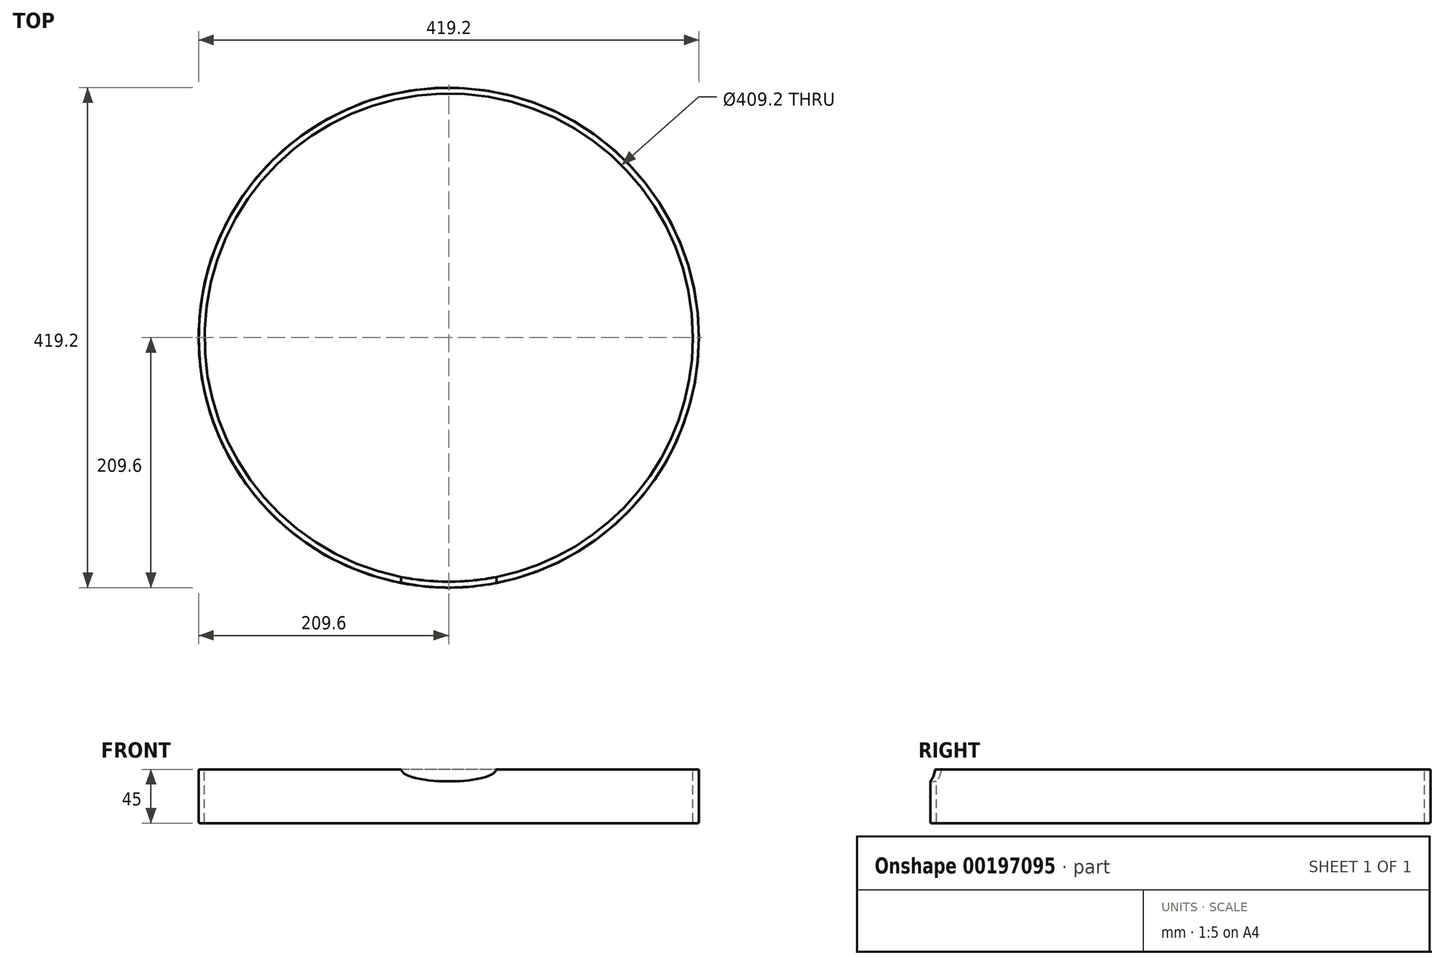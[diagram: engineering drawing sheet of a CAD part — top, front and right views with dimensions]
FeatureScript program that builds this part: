
annotation { "Feature Type Name" : "Feature", "Feature Type Description" : "" }
export const myFeature = defineFeature(function(context is Context, id is Id, definition is map)
    precondition{}
    {
        {
            var Q0;
            Q0=qCreatedBy(makeId("Front.planeOp"),FACE);
            var sketch = newSketch(context, id + "F0", { "sketchPlane" : qUnion([Q0])});
            skLineSegment(sketch, "E0", {"start": v(0, 25.64) * mm, "end": v(0, -31.1) * mm, "construction": true});
            skLineSegment(sketch, "E1", {"start": v(-208.6, 0.22) * mm, "end": v(-205.6, 0.22) * mm});
            skLineSegment(sketch, "E2", {"start": v(-204.6, -0.78) * mm, "end": v(-204.6, -43.78) * mm});
            skLineSegment(sketch, "E3", {"start": v(-209.6, -0.78) * mm, "end": v(-209.6, -43.78) * mm});
            skLineSegment(sketch, "E4", {"start": v(-208.6, -44.78) * mm, "end": v(-205.6, -44.78) * mm});
            skPoint(sketch, "E5.visualSharp", {"position": v(-204.6, 0.22) * mm});
            skArc(sketch, "E5.filletArc", {"start": v(-204.6, -0.78) * mm, "mid": v(-204.9, -0.08) * mm, "end": v(-205.6, 0.22) * mm});
            skPoint(sketch, "E6.visualSharp", {"position": v(-209.6, 0.22) * mm});
            skArc(sketch, "E6.filletArc", {"start": v(-208.6, 0.22) * mm, "mid": v(-209.3, -0.08) * mm, "end": v(-209.6, -0.78) * mm});
            skPoint(sketch, "E7.visualSharp", {"position": v(-209.6, -44.78) * mm});
            skArc(sketch, "E7.filletArc", {"start": v(-209.6, -43.78) * mm, "mid": v(-209.3, -44.5) * mm, "end": v(-208.6, -44.78) * mm});
            skPoint(sketch, "E8.visualSharp", {"position": v(-204.6, -44.78) * mm});
            skArc(sketch, "E8.filletArc", {"start": v(-205.6, -44.78) * mm, "mid": v(-204.9, -44.5) * mm, "end": v(-204.6, -43.78) * mm});
            skSolve(sketch);
        }
        {
            var Q0;
            Q0=qSketchRegion(id+"F0",true);
            var Q1;
            Q1=sQuery(id+"F0.wireOp",EDGE,"E0");
            revolve(context, id + "F1", {"entities" : qUnion([Q0]), "axis" : qUnion([Q1]), "revolveType" : RevolveType.FULL});
        }
        {
            var Q0;
            Q0=qCreatedBy(makeId("Front.planeOp"),FACE);
            var sketch = newSketch(context, id + "F2", { "sketchPlane" : qUnion([Q0])});
            skEllipse(sketch, "E9", {"center": v(0, 0.22) * mm, "majorRadius": 40 * mm, "minorRadius": 10 * mm, "majorAxis": v(1, 0)});
            skSolve(sketch);
        }
        {
            var Q0;
            Q0=makeQuery(id+"F2.imprint","IMPRINT",FACE,{"disambiguationData":[TD([[makeQuery(id+"F2.imprint","IMPRINT",EDGE,{"derivedFrom":sQuery(id+"F2.wireOp",EDGE,"E9")}),1.0]])]});
            extrude(context, id + "F3", {"entities" : qUnion([Q0]), "operationType" : NewBodyOperationType.REMOVE, "depth" : 457.2 * mm});
        }
    });
